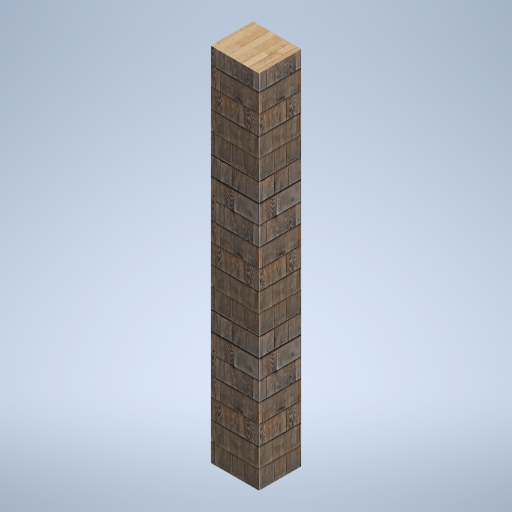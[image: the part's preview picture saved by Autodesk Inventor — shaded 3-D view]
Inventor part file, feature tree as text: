
AUTODESK INVENTOR PART (.ipt)
format: ipt  version: 2024.2 (Build 282272000, 272)  size: 353,280 bytes
history: native  units: in
note: dims shown in document units (in); Inventor stores cm internally (conversion verified against a paired STEP export)
features: other x3, sketch x1
ambient origin geometry x8: Origin, YZ Plane, XZ Plane, XY Plane, X Axis, Y Axis, Z Axis, Center Point
bodies: Solid1 (feature_tree)
feature tree (4):
  other  "support_column_02.ipt"
  other  "Solid1::support_column_02.ipt"
  other  "TaggingFeature1"
  sketch  "Sketch1"  dims[d0=0.3937in]
